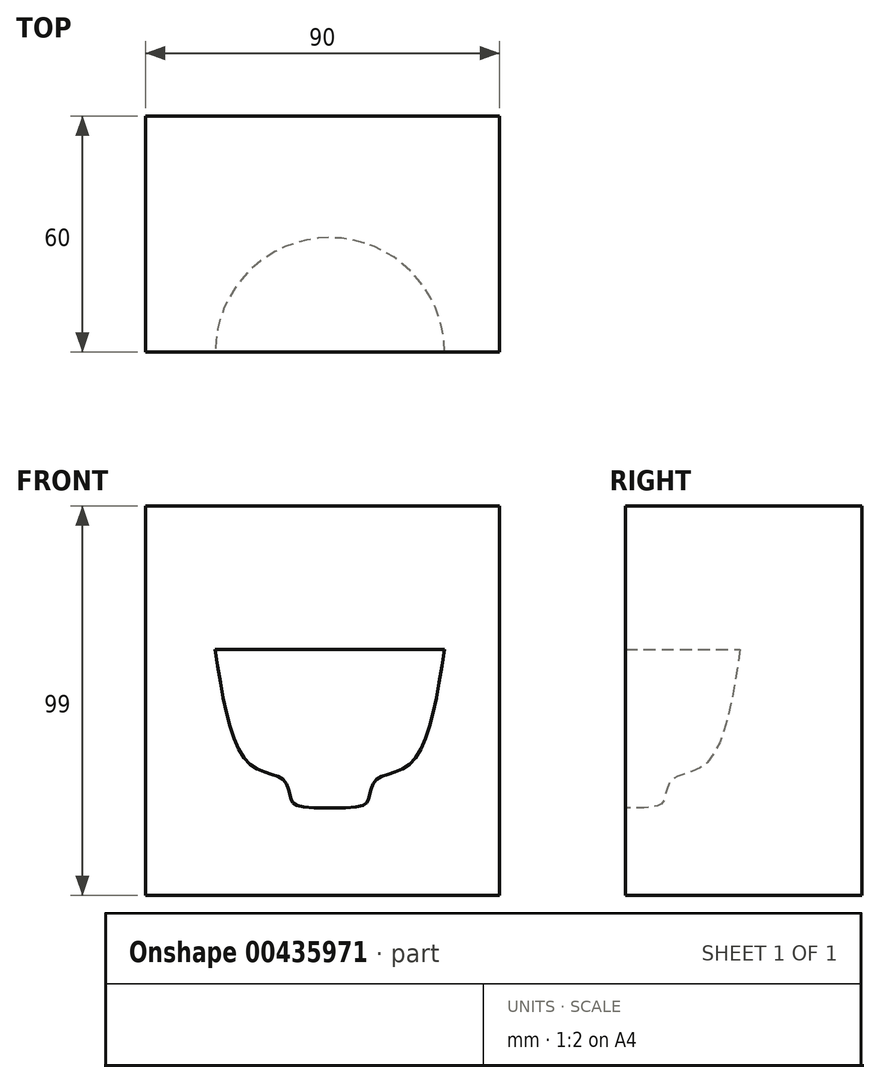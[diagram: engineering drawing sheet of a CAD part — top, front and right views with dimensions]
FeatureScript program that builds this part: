
annotation { "Feature Type Name" : "Feature", "Feature Type Description" : "" }
export const myFeature = defineFeature(function(context is Context, id is Id, definition is map)
    precondition{}
    {
        {
            var Q0;
            Q0=qCreatedBy(makeId("Front.planeOp"),FACE);
            var sketch = newSketch(context, id + "F0", { "sketchPlane" : qUnion([Q0])});
            skFitSpline(sketch, "E0", {"points": [v(28.59, -36.54) * mm, v(38.47, -34.16) * mm, v(40.38, -29.34) * mm, v(48.66, -25.58) * mm, v(57.69, 3.76) * mm], "startDerivative": vector(109.37, 0) * mm, "endDerivative": vector(14.66, 98.88) * mm});
            skLineSegment(sketch, "E1", {"start": v(28.59, -36.54) * mm, "end": v(28.59, 3.76) * mm});
            skLineSegment(sketch, "E2", {"start": v(28.59, 3.76) * mm, "end": v(57.69, 3.76) * mm});
            skLineSegment(sketch, "E3", {"start": v(0, 0) * mm, "end": v(0, -39.65) * mm, "construction": true});
            skSolve(sketch);
        }
        {
            var Q0;
            Q0=makeQuery(id+"F0.imprint","IMPRINT",FACE,{"disambiguationData":[TD([[makeQuery(id+"F0.imprint","IMPRINT",EDGE,{"derivedFrom":sQuery(id+"F0.wireOp",EDGE,"E0")}),1.0]])]});
            var Q1;
            Q1=sQuery(id+"F0.wireOp",EDGE,"E1");
            revolve(context, id + "F1", {"entities" : qUnion([Q0]), "axis" : qUnion([Q1]), "revolveType" : RevolveType.FULL});
        }
        {
            var Q0;
            Q0=qCreatedBy(makeId("Front.planeOp"),FACE);
            var sketch = newSketch(context, id + "F2", { "sketchPlane" : qUnion([Q0])});
            skLineSegment(sketch, "E4.bottom", {"start": v(-18.27, 40.25) * mm, "end": v(71.73, 40.25) * mm});
            skLineSegment(sketch, "E4.top", {"start": v(-18.27, -58.75) * mm, "end": v(71.73, -58.75) * mm});
            skLineSegment(sketch, "E4.left", {"start": v(-18.27, 40.25) * mm, "end": v(-18.27, -58.75) * mm});
            skLineSegment(sketch, "E4.right", {"start": v(71.73, 40.25) * mm, "end": v(71.73, -58.75) * mm});
            skSolve(sketch);
        }
        {
            var Q0;
            Q0 = qSketchRegion(id + "F2", true);
            extrude(context, id + "F3", {"entities" : qUnion([Q0]), "oppositeDirection" : true, "depth" : 60 * mm});
        }
        {
            var Q0;
            Q0=makeQuery(id+"F1.opRevolve","SWEPT_BODY",BODY,{"disambiguationData":[OSD([sQuery(id+"F0.wireOp",EDGE,"E0"),sQuery(id+"F0.wireOp",EDGE,"E1"),sQuery(id+"F0.wireOp",EDGE,"E2")])]});
            var Q1;
            Q1=makeQuery(id+"F3.opExtrude","SWEPT_BODY",BODY,{"disambiguationData":[OSD([sQuery(id+"F2.wireOp",EDGE,"E4.bottom"),sQuery(id+"F2.wireOp",EDGE,"E4.top"),sQuery(id+"F2.wireOp",EDGE,"E4.left"),sQuery(id+"F2.wireOp",EDGE,"E4.right")])]});
            booleanBodies(context, id + "F4", {"operationType" : BooleanOperationType.SUBTRACTION, "tools" : qUnion([Q0]), "targets" : qUnion([Q1])});
        }
    });
